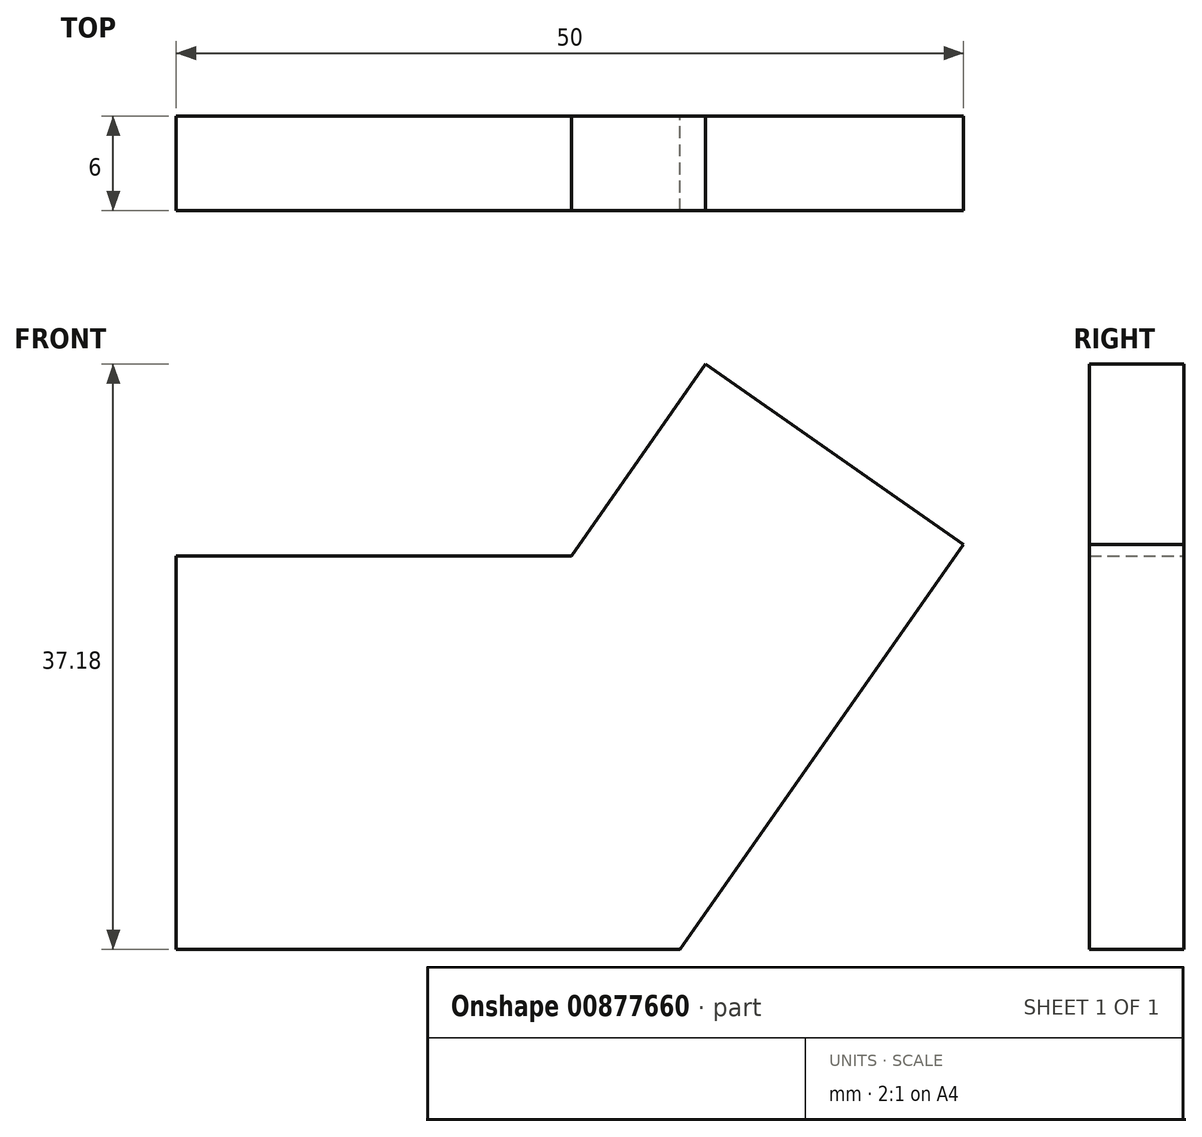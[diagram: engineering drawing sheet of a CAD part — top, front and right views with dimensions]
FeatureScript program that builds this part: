
annotation { "Feature Type Name" : "Feature", "Feature Type Description" : "" }
export const myFeature = defineFeature(function(context is Context, id is Id, definition is map)
    precondition{}
    {
        {
            var Q0;
            Q0=qCreatedBy(makeId("Front.planeOp"),FACE);
            var sketch = newSketch(context, id + "F0", { "sketchPlane" : qUnion([Q0])});
            skLineSegment(sketch, "E0", {"start": v(0, 0) * mm, "end": v(32, 0) * mm});
            skLineSegment(sketch, "E1", {"start": v(32, 0) * mm, "end": v(50, 25.7) * mm});
            skLineSegment(sketch, "E2", {"start": v(50, 25.7) * mm, "end": v(33.62, 37.18) * mm});
            skLineSegment(sketch, "E3", {"start": v(33.62, 37.18) * mm, "end": v(25.09, 25) * mm});
            skLineSegment(sketch, "E4", {"start": v(25.09, 25) * mm, "end": v(0, 25) * mm});
            skLineSegment(sketch, "E5", {"start": v(0, 25) * mm, "end": v(0, 0) * mm});
            skSolve(sketch);
        }
        {
            var Q0;
            Q0=makeQuery(id+"F0.imprint","IMPRINT",FACE,{"disambiguationData":[TD([[makeQuery(id+"F0.imprint","IMPRINT",EDGE,{"derivedFrom":sQuery(id+"F0.wireOp",EDGE,"E0")}),1.0]])]});
            extrude(context, id + "F1", {"entities" : qUnion([Q0]), "depth" : 6 * mm, "offsetDistance" : 25 * mm});
        }
    });
